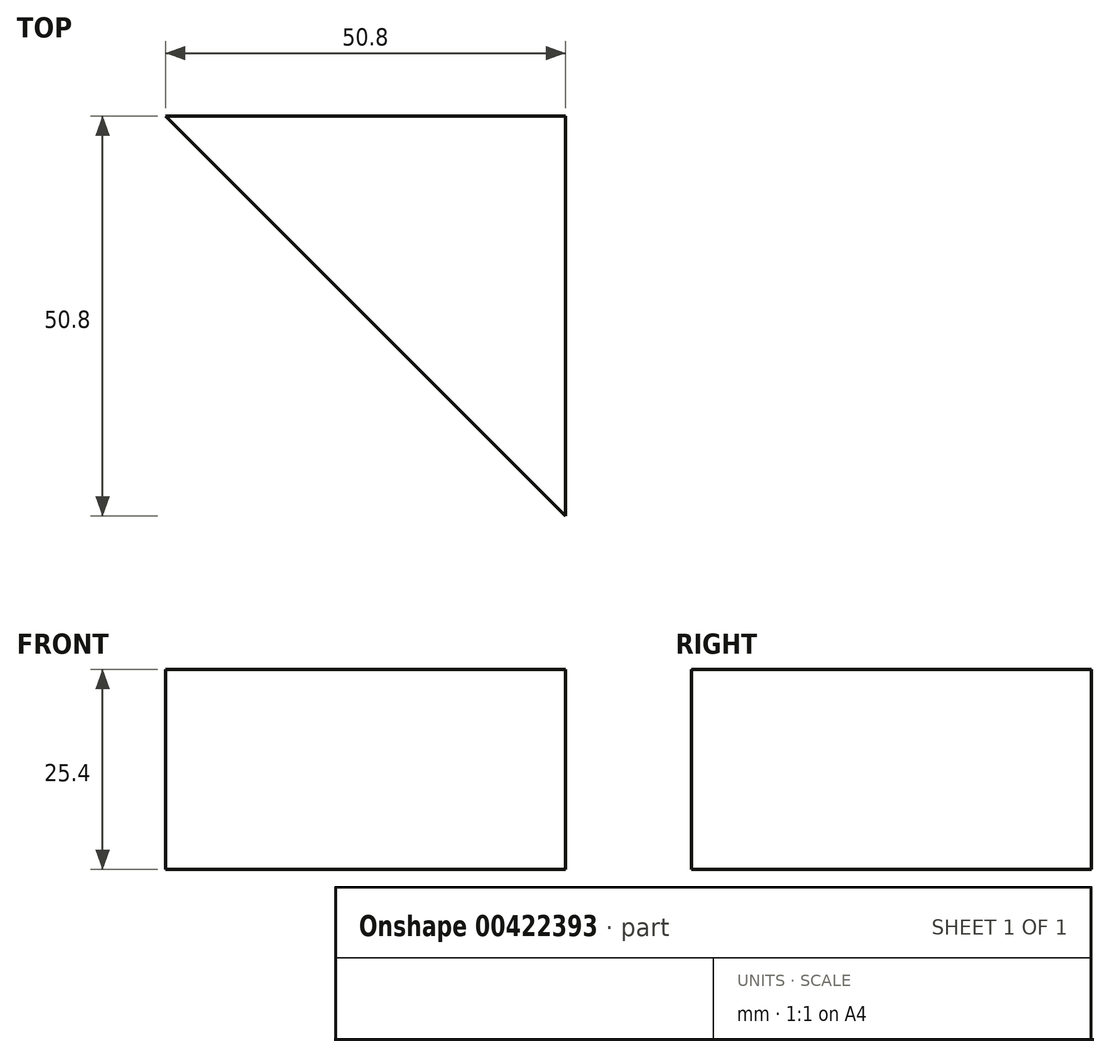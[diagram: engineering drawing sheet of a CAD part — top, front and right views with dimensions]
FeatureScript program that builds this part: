
annotation { "Feature Type Name" : "Feature", "Feature Type Description" : "" }
export const myFeature = defineFeature(function(context is Context, id is Id, definition is map)
    precondition{}
    {
        {
            var Q0;
            Q0=qCreatedBy(makeId("Top.planeOp"),FACE);
            var sketch = newSketch(context, id + "F0", { "sketchPlane" : qUnion([Q0])});
            skLineSegment(sketch, "E0", {"start": v(0, 0) * mm, "end": v(0, -50.8) * mm});
            skLineSegment(sketch, "E1", {"start": v(0, 0) * mm, "end": v(-50.8, 0) * mm});
            skLineSegment(sketch, "E2", {"start": v(-50.8, 0) * mm, "end": v(0, -50.8) * mm});
            skSolve(sketch);
        }
        {
            var Q0;
            Q0 = qSketchRegion(id + "F0", true);
            extrude(context, id + "F1", {"entities" : qUnion([Q0]), "depth" : 25.4 * mm});
        }
    });
